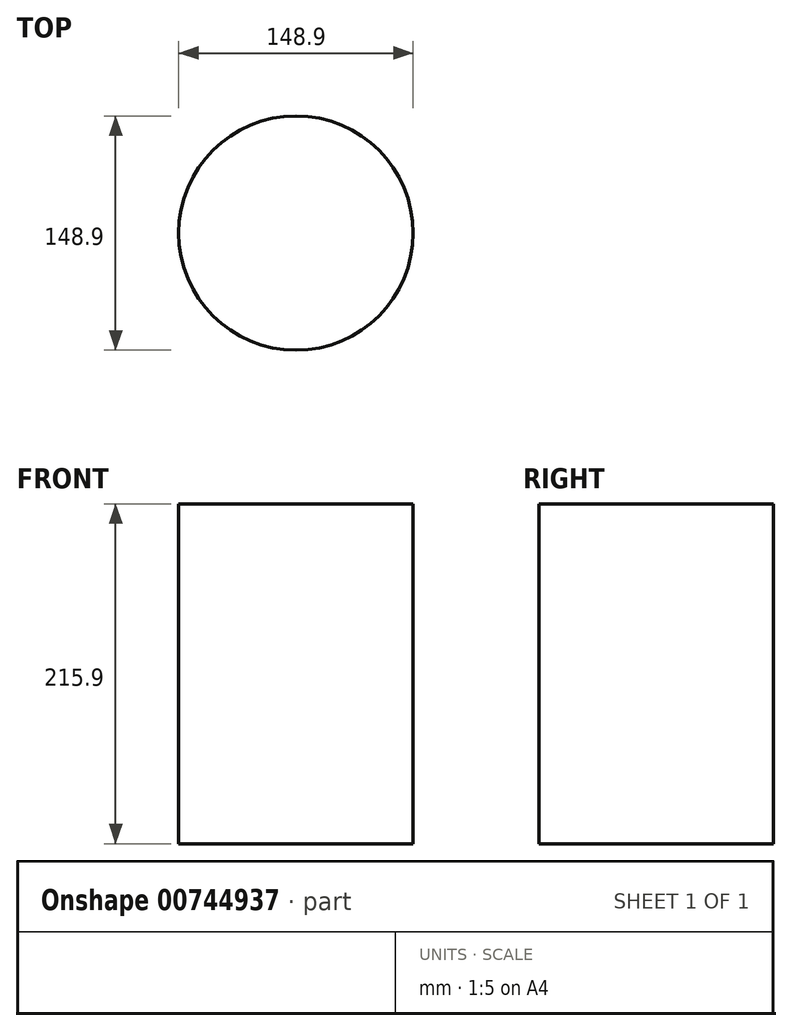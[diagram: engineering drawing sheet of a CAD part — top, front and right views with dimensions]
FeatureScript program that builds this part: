
annotation { "Feature Type Name" : "Feature", "Feature Type Description" : "" }
export const myFeature = defineFeature(function(context is Context, id is Id, definition is map)
    precondition{}
    {
        {
            var Q0;
            Q0=qCreatedBy(makeId("Top.planeOp"),FACE);
            var sketch = newSketch(context, id + "F0", { "sketchPlane" : qUnion([Q0])});
            skCircle(sketch, "E0", {"center": v(0, 0) * mm, "radius": 74.45 * mm});
            skSolve(sketch);
        }
        {
            var Q0;
            Q0=sQuery(id+"F0.wireOp",EDGE,"E0");
            extrude(context, id + "F1", {"bodyType" : ToolBodyType.SURFACE, "surfaceEntities" : qUnion([Q0]), "depth" : 107.95 * mm, "offsetDistance" : 25.4 * mm, "hasSecondDirection" : true, "secondDirectionOppositeDirection" : true, "secondDirectionDepth" : 107.95 * mm});
        }
    });
